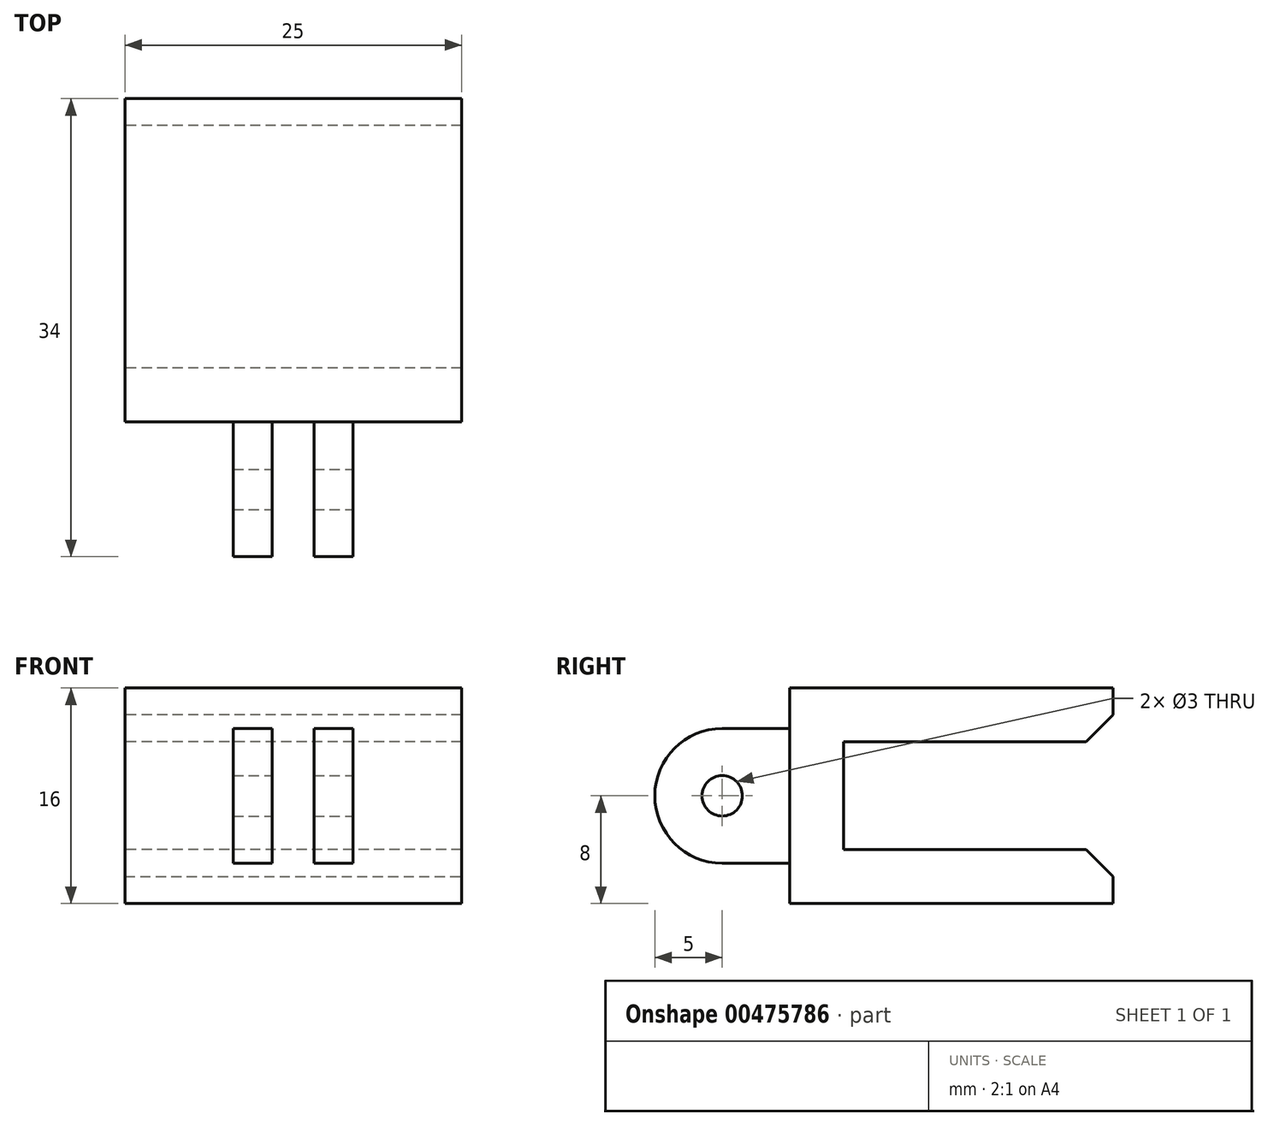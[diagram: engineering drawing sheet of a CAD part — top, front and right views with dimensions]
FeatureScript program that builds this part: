
annotation { "Feature Type Name" : "Feature", "Feature Type Description" : "" }
export const myFeature = defineFeature(function(context is Context, id is Id, definition is map)
    precondition{}
    {
        {
            var Q0;
            Q0=qCreatedBy(makeId("Right.planeOp"),FACE);
            var sketch = newSketch(context, id + "F0", { "sketchPlane" : qUnion([Q0])});
            skLineSegment(sketch, "E0", {"start": v(0, 0) * mm, "end": v(-24, 0) * mm});
            skLineSegment(sketch, "E1", {"start": v(-24, 0) * mm, "end": v(-24, 16) * mm});
            skLineSegment(sketch, "E2", {"start": v(-24, 16) * mm, "end": v(0, 16) * mm});
            skLineSegment(sketch, "E3", {"start": v(0, 16) * mm, "end": v(0, 12) * mm});
            skLineSegment(sketch, "E4", {"start": v(0, 12) * mm, "end": v(-20, 12) * mm});
            skLineSegment(sketch, "E5", {"start": v(-20, 12) * mm, "end": v(-20, 4) * mm});
            skLineSegment(sketch, "E6", {"start": v(-20, 4) * mm, "end": v(0, 4) * mm});
            skLineSegment(sketch, "E7", {"start": v(0, 4) * mm, "end": v(0, 0) * mm});
            skSolve(sketch);
        }
        {
            var Q0;
            Q0=makeQuery(id+"F0.imprint","IMPRINT",FACE,{"disambiguationData":[TD([[makeQuery(id+"F0.imprint","IMPRINT",EDGE,{"derivedFrom":sQuery(id+"F0.wireOp",EDGE,"E0")}),-1.0]])]});
            extrude(context, id + "F1", {"entities" : qUnion([Q0]), "depth" : 25 * mm});
        }
        {
            var Q0;
            Q0=makeQuery(id+"F1.opExtrude","SWEPT_FACE",FACE,{"disambiguationData":[OSD([sQuery(id+"F0.wireOp",EDGE,"E1")])]});
            var sketch = newSketch(context, id + "F2", { "sketchPlane" : qUnion([Q0])});
            skLineSegment(sketch, "E8", {"start": v(12.5, 16) * mm, "end": v(12.5, 0) * mm, "construction": true});
            skLineSegment(sketch, "E9", {"start": v(25, 8) * mm, "end": v(0, 8) * mm, "construction": true});
            skLineSegment(sketch, "E10.bottom", {"start": v(14.05, 13) * mm, "end": v(16.95, 13) * mm});
            skLineSegment(sketch, "E10.top", {"start": v(14.05, 3) * mm, "end": v(16.95, 3) * mm});
            skLineSegment(sketch, "E10.left", {"start": v(14.05, 13) * mm, "end": v(14.05, 3) * mm});
            skLineSegment(sketch, "E10.right", {"start": v(16.95, 13) * mm, "end": v(16.95, 3) * mm});
            skPoint(sketch, "E10.middle", {"position": v(15.5, 8) * mm});
            skLineSegment(sketch, "E11.bottom", {"start": v(10.95, 13) * mm, "end": v(8.05, 13) * mm});
            skLineSegment(sketch, "E11.top", {"start": v(10.95, 3) * mm, "end": v(8.05, 3) * mm});
            skLineSegment(sketch, "E11.left", {"start": v(10.95, 13) * mm, "end": v(10.95, 3) * mm});
            skLineSegment(sketch, "E11.right", {"start": v(8.05, 13) * mm, "end": v(8.05, 3) * mm});
            skPoint(sketch, "E11.middle", {"position": v(9.5, 8) * mm});
            skSolve(sketch);
        }
        {
            var Q0;
            Q0=makeQuery(id+"F2.imprint","IMPRINT",FACE,{"disambiguationData":[TD([[makeQuery(id+"F2.imprint","IMPRINT",EDGE,{"derivedFrom":sQuery(id+"F2.wireOp",EDGE,"E11.bottom")}),1.0]])]});
            var Q1;
            Q1=makeQuery(id+"F2.imprint","IMPRINT",FACE,{"disambiguationData":[TD([[makeQuery(id+"F2.imprint","IMPRINT",EDGE,{"derivedFrom":sQuery(id+"F2.wireOp",EDGE,"E10.bottom")}),-1.0]])]});
            extrude(context, id + "F3", {"entities" : qUnion([Q0, Q1]), "operationType" : NewBodyOperationType.ADD, "depth" : 10 * mm});
        }
        {
            var Q0;
            Q0=makeQuery(id+"F3.opExtrude","SWEPT_FACE",FACE,{"disambiguationData":[OSD([sQuery(id+"F2.wireOp",EDGE,"E10.right")])]});
            var sketch = newSketch(context, id + "F4", { "sketchPlane" : qUnion([Q0])});
            skLineSegment(sketch, "E12", {"start": v(-29, 13) * mm, "end": v(-29, 3) * mm, "construction": true});
            skLineSegment(sketch, "E13", {"start": v(-24, 8) * mm, "end": v(-34, 8) * mm, "construction": true});
            skArc(sketch, "E14", {"start": v(-29, 13) * mm, "mid": v(-34, 8) * mm, "end": v(-29, 3) * mm});
            skCircle(sketch, "E15", {"center": v(-29, 8) * mm, "radius": 1.5 * mm});
            skLineSegment(sketch, "E16", {"start": v(-29, 13) * mm, "end": v(-34, 13) * mm});
            skLineSegment(sketch, "E17", {"start": v(-34, 13) * mm, "end": v(-34, 3) * mm});
            skLineSegment(sketch, "E18", {"start": v(-34, 3) * mm, "end": v(-29, 3) * mm});
            skSolve(sketch);
        }
        {
            var Q0;
            {var subQ0=sQuery(id+"F4.wireOp",EDGE,"E16");Q0=makeQuery(id+"F4.imprint","IMPRINT",FACE,{"disambiguationData":[TD([[makeQuery(id+"F4.imprint","IMPRINT",EDGE,{"derivedFrom":subQ0}),-1.0]])]});}
            var Q1;
            {var subQ0=sQuery(id+"F4.wireOp",EDGE,"E18");Q1=makeQuery(id+"F4.imprint","IMPRINT",FACE,{"disambiguationData":[TD([[makeQuery(id+"F4.imprint","IMPRINT",EDGE,{"derivedFrom":subQ0}),1.0]])]});}
            var Q2;
            Q2=makeQuery(id+"F4.imprint","IMPRINT",FACE,{"disambiguationData":[TD([[makeQuery(id+"F4.imprint","IMPRINT",EDGE,{"derivedFrom":sQuery(id+"F4.wireOp",EDGE,"E15")}),1.0]])]});
            extrude(context, id + "F5", {"entities" : qUnion([Q0, Q1, Q2]), "operationType" : NewBodyOperationType.REMOVE, "oppositeDirection" : true, "depth" : 9 * mm});
        }
        {
            var Q0;
            Q0=makeQuery(id+"F1.opExtrude","SWEPT_EDGE",EDGE,{"disambiguationData":[OSD([sQuery(id+"F0.wireOp",EDGE,"E3"),sQuery(id+"F0.wireOp",EDGE,"E4")])]});
            var Q1;
            Q1=makeQuery(id+"F1.opExtrude","SWEPT_EDGE",EDGE,{"disambiguationData":[OSD([sQuery(id+"F0.wireOp",EDGE,"E6"),sQuery(id+"F0.wireOp",EDGE,"E7")])]});
            chamfer(context, id + "F6", {"entities" : qUnion([Q0, Q1]), "width" : 2 * mm, "tangentPropagation" : true});
        }
    });
